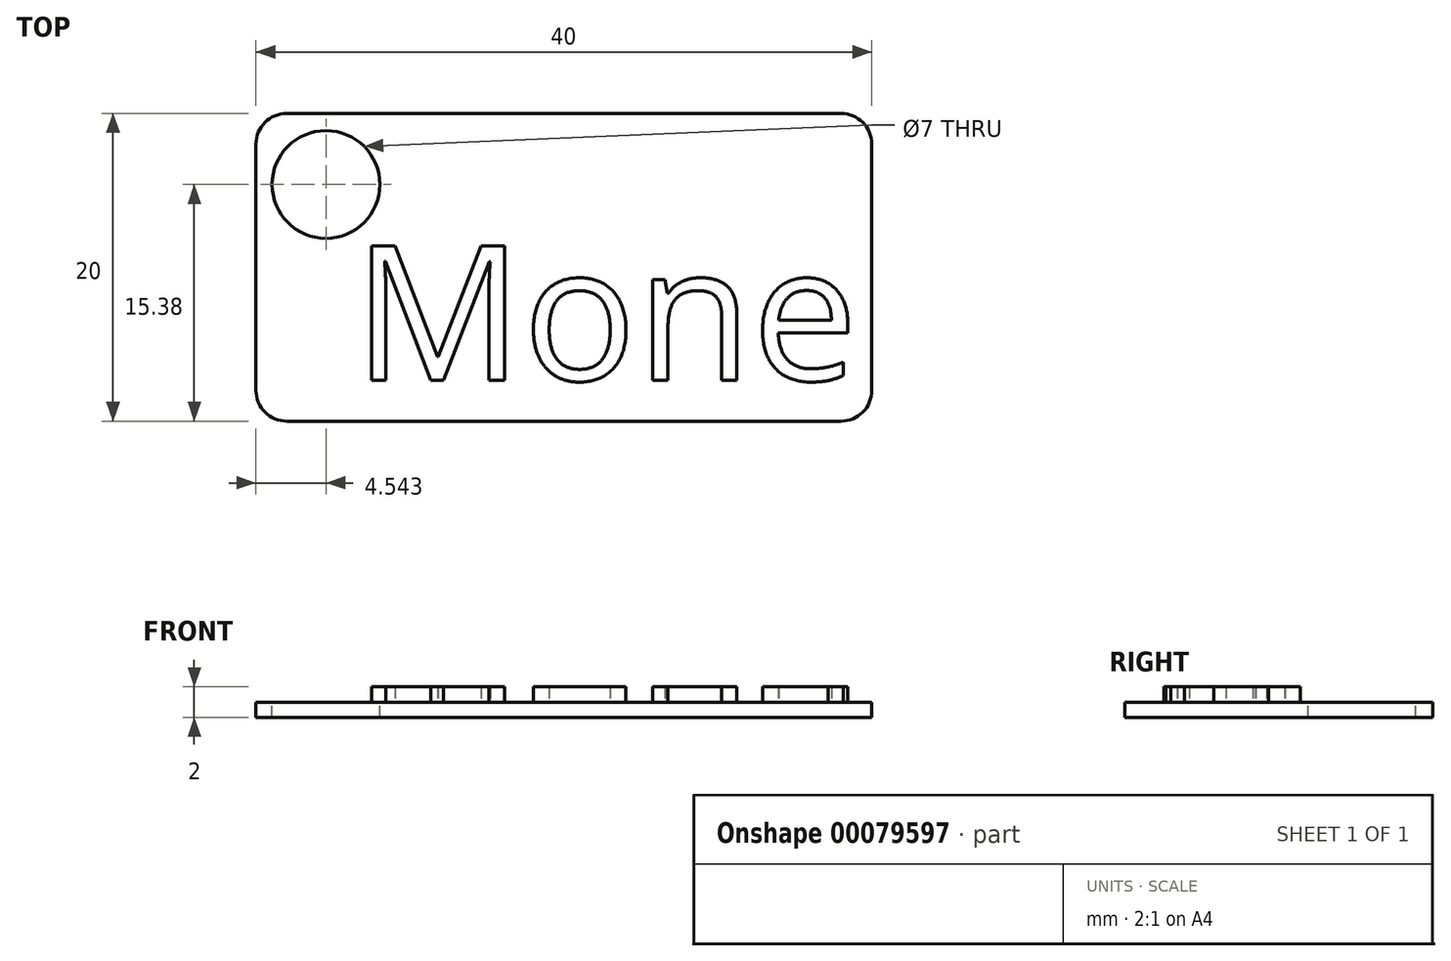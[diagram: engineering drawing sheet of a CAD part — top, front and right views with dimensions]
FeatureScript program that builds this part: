
annotation { "Feature Type Name" : "Feature", "Feature Type Description" : "" }
export const myFeature = defineFeature(function(context is Context, id is Id, definition is map)
    precondition{}
    {
        {
            var Q0;
            Q0=qCreatedBy(makeId("Top.planeOp"),FACE);
            var sketch = newSketch(context, id + "F0", { "sketchPlane" : qUnion([Q0])});
            skLineSegment(sketch, "E0.bottom", {"start": v(-20, -10) * mm, "end": v(20, -10) * mm});
            skLineSegment(sketch, "E0.top", {"start": v(-20, 10) * mm, "end": v(20, 10) * mm});
            skLineSegment(sketch, "E0.left", {"start": v(-20, -10) * mm, "end": v(-20, 10) * mm});
            skLineSegment(sketch, "E0.right", {"start": v(20, -10) * mm, "end": v(20, 10) * mm});
            skPoint(sketch, "E0.middle", {"position": v(0, 0) * mm});
            skSolve(sketch);
        }
        {
            var Q0;
            Q0 = qSketchRegion(id + "F0", true);
            extrude(context, id + "F1", {"entities" : qUnion([Q0]), "depth" : 1 * mm});
        }
        {
            var Q0;
            Q0=makeQuery(id+"F1.opExtrude","CAP_FACE",FACE,{"disambiguationData":[OSD([sQuery(id+"F0.wireOp",EDGE,"E0.bottom"),sQuery(id+"F0.wireOp",EDGE,"E0.top"),sQuery(id+"F0.wireOp",EDGE,"E0.left"),sQuery(id+"F0.wireOp",EDGE,"E0.right")])],"isStart":false});
            var sketch = newSketch(context, id + "F2", { "sketchPlane" : qUnion([Q0])});
            skText(sketch, "E1", { "text": "Mone", "fontName": "OpenSans-Regular.ttf"});
            const initialGuessF2  = {"E1": [-0.0137, -0.00734, 1, 0, 0.0088]};
            skSetInitialGuess(sketch, initialGuessF2);
            skSolve(sketch);
        }
        {
            var Q0;
            Q0=makeQuery(id+"F2.imprint","IMPRINT",FACE,{"disambiguationData":[TD([[makeQuery(id+"F2.imprint","IMPRINT",EDGE,{"derivedFrom":sQuery(id+"F2.wireOp",EDGE,"E1.sketch_text.stroke-0")}),-1.0]])]});
            var Q1;
            Q1=makeQuery(id+"F2.imprint","IMPRINT",FACE,{"disambiguationData":[TD([[makeQuery(id+"F2.imprint","IMPRINT",EDGE,{"derivedFrom":sQuery(id+"F2.wireOp",EDGE,"E1.sketch_text.stroke-35")}),-1.0]])]});
            var Q2;
            Q2=makeQuery(id+"F2.imprint","IMPRINT",FACE,{"disambiguationData":[TD([[makeQuery(id+"F2.imprint","IMPRINT",EDGE,{"derivedFrom":sQuery(id+"F2.wireOp",EDGE,"E1.sketch_text.stroke-18")}),-1.0]])]});
            var Q3;
            Q3=makeQuery(id+"F2.imprint","IMPRINT",FACE,{"disambiguationData":[TD([[makeQuery(id+"F2.imprint","IMPRINT",EDGE,{"derivedFrom":sQuery(id+"F2.wireOp",EDGE,"E1.sketch_text.stroke-52")}),-1.0]])]});
            extrude(context, id + "F3", {"entities" : qUnion([Q0, Q1, Q2, Q3]), "operationType" : NewBodyOperationType.ADD, "depth" : 1 * mm});
        }
        {
            var Q0;
            {var subQ0=sQuery(id+"F0.wireOp",EDGE,"E0.top");var subQ1=sQuery(id+"F0.wireOp",EDGE,"E0.right");var subQ2=sQuery(id+"F0.wireOp",EDGE,"E0.bottom");var subQ3=sQuery(id+"F0.wireOp",EDGE,"E0.left");Q0=makeQuery(id+"F3.boolean.opBoolean","SPLIT",FACE,{"disambiguationData":[TD([makeQuery(id+"F1.opExtrude","SWEPT_FACE",FACE,{"disambiguationData":[OSD([subQ2])]})])],"derivedFrom":makeQuery(id+"F1.opExtrude","CAP_FACE",FACE,{"disambiguationData":[OSD([subQ2,subQ0,subQ3,subQ1])],"isStart":false})});}
            var sketch = newSketch(context, id + "F4", { "sketchPlane" : qUnion([Q0])});
            skPoint(sketch, "E2", {"position": v(-15.46, 5.38) * mm});
            skSolve(sketch);
        }
        {
            var Q0;
            Q0=makeQuery(id+"F1.opExtrude","SWEPT_EDGE",EDGE,{"disambiguationData":[OSD([sQuery(id+"F0.wireOp",EDGE,"E0.top"),sQuery(id+"F0.wireOp",EDGE,"E0.left")])]});
            var Q1;
            Q1=makeQuery(id+"F1.opExtrude","SWEPT_EDGE",EDGE,{"disambiguationData":[OSD([sQuery(id+"F0.wireOp",EDGE,"E0.bottom"),sQuery(id+"F0.wireOp",EDGE,"E0.left")])]});
            var Q2;
            Q2=makeQuery(id+"F1.opExtrude","SWEPT_EDGE",EDGE,{"disambiguationData":[OSD([sQuery(id+"F0.wireOp",EDGE,"E0.bottom"),sQuery(id+"F0.wireOp",EDGE,"E0.right")])]});
            var Q3;
            Q3=makeQuery(id+"F1.opExtrude","SWEPT_EDGE",EDGE,{"disambiguationData":[OSD([sQuery(id+"F0.wireOp",EDGE,"E0.top"),sQuery(id+"F0.wireOp",EDGE,"E0.right")])]});
            fillet(context, id + "F5", {"entities" : qUnion([Q0, Q1, Q2, Q3]), "radius" : 2 * mm, "tangentPropagation" : true, "allowEdgeOverflow" : false});
        }
        {
            var Q0;
            Q0=sQuery(id+"F4.wireOp",VERTEX,"E2");
            var Q1;
            Q1=makeQuery(id+"F1.opExtrude","SWEPT_BODY",BODY,{"disambiguationData":[OSD([sQuery(id+"F0.wireOp",EDGE,"E0.bottom"),sQuery(id+"F0.wireOp",EDGE,"E0.top"),sQuery(id+"F0.wireOp",EDGE,"E0.left"),sQuery(id+"F0.wireOp",EDGE,"E0.right")])]});
            hole(context, id + "F6", {"style" : HoleStyle.SIMPLE, "endStyle" : HoleEndStyle.BLIND, "holeDiameter" : 7 * mm, "holeDepth" : 50 * mm, "locations" : qUnion([Q0]), "scope" : qUnion([Q1])});
        }
    });
